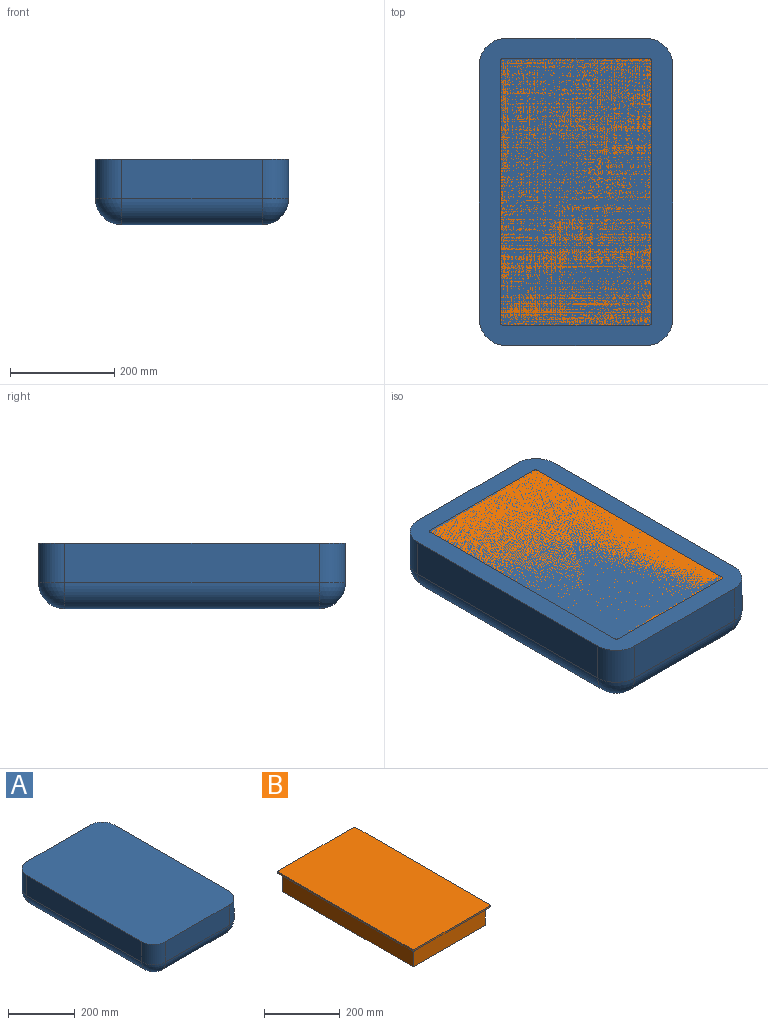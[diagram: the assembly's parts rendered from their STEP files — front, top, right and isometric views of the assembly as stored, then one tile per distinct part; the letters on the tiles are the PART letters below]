
ASSEMBLY  parts=2 mates=1
PART A: 18 faces, bbox 370x588x125 mm
  f0: plane 270x75mm, normal (0,1,0), area 20250mm2, adj f5,f11,f15,f17
  f1: plane 488x75mm, normal (-1,0,0), area 36600mm2, adj f5,f8,f14,f17
  f2: plane 270x75mm, normal (0,-1,0), area 20250mm2, adj f5,f6,f8,f9
  f3: plane 488x75mm, normal (1,0,0), area 36600mm2, adj f5,f6,f10,f11
  f4: plane 488x270mm, normal (0,0,-1), area 131760mm2, adj f9,f10,f14,f15
  f5: plane 588x370mm, normal (0,0,1), area 215414mm2, adj f0,f1,f2,f3,f6,f8,f11,f17
  f6: cylinder r=50mm len=75mm, axis (0,0,-1), area 5890.5mm2, adj f2,f3,f5,f7
  f7: sphere r=50mm, area 3927mm2, adj f6,f9,f10
  f8: cylinder r=50mm len=75mm, axis (0,0,1), area 5890.5mm2, adj f1,f2,f5,f12
  f9: cylinder r=50mm len=270mm, axis (-1,0,0), area 21205.8mm2, adj f2,f4,f7,f12
  f10: cylinder r=50mm len=488mm, axis (0,-1,0), area 38327.4mm2, adj f3,f4,f7,f13
  f11: cylinder r=50mm len=75mm, axis (0,0,1), area 5890.5mm2, adj f0,f3,f5,f13
  f12: sphere r=50mm, area 3927mm2, adj f8,f9,f14
  f13: sphere r=50mm, area 3927mm2, adj f10,f11,f15
  f14: cylinder r=50mm len=488mm, axis (0,1,0), area 38327.4mm2, adj f1,f4,f12,f16
  f15: cylinder r=50mm len=270mm, axis (1,0,0), area 21205.8mm2, adj f0,f4,f13,f16
  f16: sphere r=50mm, area 3927mm2, adj f14,f15,f17
  f17: cylinder r=50mm len=75mm, axis (0,0,-1), area 5890.5mm2, adj f0,f1,f5,f16
PART B: 15 faces, bbox 290x510x65 mm
  f0: plane 270x60mm, normal (0,-1,0), area 16200mm2, adj f1,f3,f4,f5
  f1: plane 488x60mm, normal (1,0,0), area 29280mm2, adj f0,f2,f4,f5
  f2: plane 270x60mm, normal (0,1,0), area 16200mm2, adj f1,f3,f4,f5
  f3: plane 488x60mm, normal (-1,0,0), area 29280mm2, adj f0,f2,f4,f5
  f4: plane 488x270mm, normal (0,0,-1), area 131760mm2, adj f0,f1,f2,f3
  f5: plane 510x290mm, normal (0,0,-1), area 16118.5mm2, adj f0,f1,f2,f3,f6,f7,f8,f9
  f6: plane 280x5mm, normal (0,1,0), area 1400mm2, adj f5,f10,f11,f14
  f7: plane 500x5mm, normal (-1,0,0), area 2500mm2, adj f5,f10,f11,f12
  f8: plane 280x5mm, normal (0,-1,0), area 1400mm2, adj f5,f10,f12,f13
  f9: plane 500x5mm, normal (1,0,0), area 2500mm2, adj f5,f10,f13,f14
  f10: plane 510x290mm, normal (0,0,1), area 147878.5mm2, adj f6,f7,f8,f9,f11,f12,f13,f14
  f11: cylinder r=5mm len=5mm, axis (0,0,-1), area 39.3mm2, adj f5,f6,f7,f10
  f12: cylinder r=5mm len=5mm, axis (0,0,1), area 39.3mm2, adj f5,f7,f8,f10
  f13: cylinder r=5mm len=5mm, axis (0,0,-1), area 39.3mm2, adj f5,f8,f9,f10
  f14: cylinder r=5mm len=5mm, axis (0,0,1), area 39.3mm2, adj f5,f6,f9,f10
PLACE A at identity fixed
PLACE B at identity
MATE fastened A.f5 <-> B.f10  axis (0,0,1) through (0,0,0)mm
